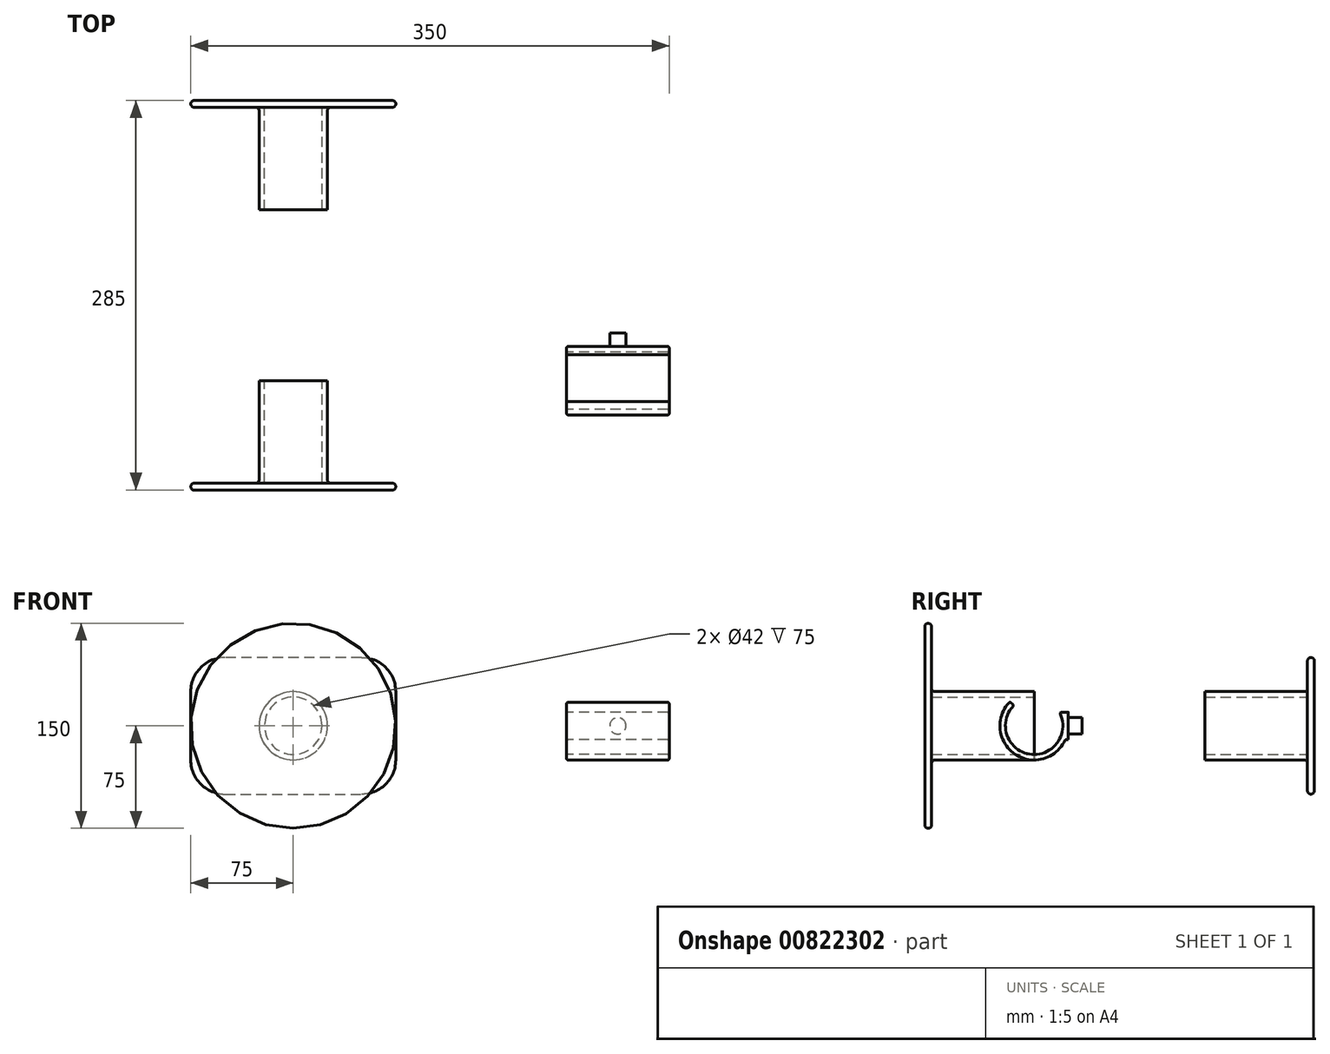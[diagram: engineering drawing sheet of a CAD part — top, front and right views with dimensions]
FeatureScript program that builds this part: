
annotation { "Feature Type Name" : "Feature", "Feature Type Description" : "" }
export const myFeature = defineFeature(function(context is Context, id is Id, definition is map)
    precondition{}
    {
        {
            var Q0;
            Q0=qCreatedBy(makeId("Front.planeOp"),FACE);
            var sketch = newSketch(context, id + "F0", { "sketchPlane" : qUnion([Q0])});
            skCircle(sketch, "E0", {"center": v(0, 0) * mm, "radius": 21 * mm});
            skCircle(sketch, "E1", {"center": v(0, 0) * mm, "radius": 25 * mm});
            skSolve(sketch);
        }
        {
            var Q0;
            Q0 = qSketchRegion(id + "F0", true);
            extrude(context, id + "F1", {"entities" : qUnion([Q0]), "depth" : 75 * mm, "offsetDistance" : 25 * mm});
        }
        {
            var Q0;
            Q0=makeQuery(id+"F1.opExtrude","CAP_FACE",FACE,{"disambiguationData":[OSD([sQuery(id+"F0.wireOp",EDGE,"E0"),sQuery(id+"F0.wireOp",EDGE,"E1")])],"isStart":false});
            var sketch = newSketch(context, id + "F2", { "sketchPlane" : qUnion([Q0])});
            skCircle(sketch, "E2", {"center": v(0, 0) * mm, "radius": 75 * mm});
            skSolve(sketch);
        }
        {
            var Q0;
            Q0 = qSketchRegion(id + "F2", true);
            extrude(context, id + "F3", {"entities" : qUnion([Q0]), "operationType" : NewBodyOperationType.ADD, "depth" : 5 * mm, "offsetDistance" : 25 * mm});
        }
        {
            var Q0;
            Q0=makeQuery(id+"F3.opExtrude","CAP_FACE",FACE,{"disambiguationData":[OSD([sQuery(id+"F2.wireOp",EDGE,"E2")])],"isStart":false});
            var Q1;
            {var subQ0=sQuery(id+"F2.wireOp",EDGE,"E2");Q1=makeQuery(id+"F3.boolean.opBoolean","SPLIT",FACE,{"disambiguationData":[TD([makeQuery(id+"F1.opExtrude","SWEPT_FACE",FACE,{"disambiguationData":[OSD([sQuery(id+"F0.wireOp",EDGE,"E1")])]})])],"derivedFrom":makeQuery(id+"F3.opExtrude","CAP_FACE",FACE,{"disambiguationData":[OSD([subQ0])],"isStart":true})});}
            fillet(context, id + "F4", {"entities" : qUnion([Q0, Q1]), "radius" : 2.5 * mm, "tangentPropagation" : true, "allowEdgeOverflow" : false});
        }
        {
            var Q0;
            Q0=qCreatedBy(makeId("Front.planeOp"),FACE);
            cPlane(context, id + "F5", {"entities" : qUnion([Q0]), "cplaneType" : CPlaneType.OFFSET, "offset" : 200 * mm, "oppositeDirection" : true, "width" : 150 * mm, "height" : 150 * mm});
        }
        {
            var Q0;
            Q0=qCreatedBy(id+"F5.planeOp",FACE);
            var sketch = newSketch(context, id + "F6", { "sketchPlane" : qUnion([Q0])});
            skCircle(sketch, "E3", {"center": v(0, 0) * mm, "radius": 21 * mm});
            skCircle(sketch, "E4", {"center": v(0, 0) * mm, "radius": 25 * mm});
            skSolve(sketch);
        }
        {
            var Q0;
            Q0 = qSketchRegion(id + "F6", true);
            extrude(context, id + "F7", {"entities" : qUnion([Q0]), "depth" : 75 * mm, "offsetDistance" : 25 * mm});
        }
        {
            var Q0;
            Q0=makeQuery(id+"F7.opExtrude","CAP_FACE",FACE,{"disambiguationData":[OSD([sQuery(id+"F6.wireOp",EDGE,"E3"),sQuery(id+"F6.wireOp",EDGE,"E4")])],"isStart":true});
            var sketch = newSketch(context, id + "F8", { "sketchPlane" : qUnion([Q0])});
            skLineSegment(sketch, "E5.bottom", {"start": v(-50, -50) * mm, "end": v(50, -50) * mm});
            skLineSegment(sketch, "E5.top", {"start": v(-50, 50) * mm, "end": v(50, 50) * mm});
            skLineSegment(sketch, "E5.left", {"start": v(-75, -25) * mm, "end": v(-75, 25) * mm});
            skLineSegment(sketch, "E5.right", {"start": v(75, -25) * mm, "end": v(75, 25) * mm});
            skPoint(sketch, "E5.middle", {"position": v(0, 0) * mm});
            skPoint(sketch, "E6.visualSharp", {"position": v(-75, 50) * mm});
            skArc(sketch, "E6.filletArc", {"start": v(-50, 50) * mm, "mid": v(-67.68, 42.68) * mm, "end": v(-75, 25) * mm});
            skPoint(sketch, "E7.visualSharp", {"position": v(-75, -50) * mm});
            skArc(sketch, "E7.filletArc", {"start": v(-75, -25) * mm, "mid": v(-67.68, -42.68) * mm, "end": v(-50, -50) * mm});
            skPoint(sketch, "E8.visualSharp", {"position": v(75, -50) * mm});
            skArc(sketch, "E8.filletArc", {"start": v(50, -50) * mm, "mid": v(67.68, -42.68) * mm, "end": v(75, -25) * mm});
            skPoint(sketch, "E9.visualSharp", {"position": v(75, 50) * mm});
            skArc(sketch, "E9.filletArc", {"start": v(75, 25) * mm, "mid": v(67.68, 42.68) * mm, "end": v(50, 50) * mm});
            skSolve(sketch);
        }
        {
            var Q0;
            Q0 = qSketchRegion(id + "F8", true);
            extrude(context, id + "F9", {"entities" : qUnion([Q0]), "operationType" : NewBodyOperationType.ADD, "depth" : 5 * mm, "offsetDistance" : 25 * mm});
        }
        {
            var Q0;
            Q0=makeQuery(id+"F9.opExtrude","CAP_FACE",FACE,{"disambiguationData":[OSD([sQuery(id+"F8.wireOp",EDGE,"E5.bottom"),sQuery(id+"F8.wireOp",EDGE,"E5.top"),sQuery(id+"F8.wireOp",EDGE,"E5.left"),sQuery(id+"F8.wireOp",EDGE,"E5.right"),sQuery(id+"F8.wireOp",EDGE,"E6.filletArc"),sQuery(id+"F8.wireOp",EDGE,"E7.filletArc"),sQuery(id+"F8.wireOp",EDGE,"E8.filletArc"),sQuery(id+"F8.wireOp",EDGE,"E9.filletArc")])],"isStart":false});
            var Q1;
            {var subQ0=sQuery(id+"F8.wireOp",EDGE,"E5.left");var subQ1=sQuery(id+"F8.wireOp",EDGE,"E5.top");var subQ2=sQuery(id+"F8.wireOp",EDGE,"E5.bottom");var subQ3=sQuery(id+"F8.wireOp",EDGE,"E5.right");var subQ4=sQuery(id+"F8.wireOp",EDGE,"E6.filletArc");var subQ5=sQuery(id+"F8.wireOp",EDGE,"E7.filletArc");var subQ6=sQuery(id+"F8.wireOp",EDGE,"E8.filletArc");var subQ7=sQuery(id+"F8.wireOp",EDGE,"E9.filletArc");Q1=makeQuery(id+"F9.boolean.opBoolean","SPLIT",FACE,{"disambiguationData":[TD([makeQuery(id+"F7.opExtrude","SWEPT_FACE",FACE,{"disambiguationData":[OSD([sQuery(id+"F6.wireOp",EDGE,"E4")])]})])],"derivedFrom":makeQuery(id+"F9.opExtrude","CAP_FACE",FACE,{"disambiguationData":[OSD([subQ2,subQ1,subQ0,subQ3,subQ4,subQ5,subQ6,subQ7])],"isStart":true})});}
            fillet(context, id + "F10", {"entities" : qUnion([Q0, Q1]), "radius" : 2.5 * mm, "tangentPropagation" : true, "allowEdgeOverflow" : false});
        }
        {
            var Q0;
            Q0=qCreatedBy(makeId("Right.planeOp"),FACE);
            cPlane(context, id + "F11", {"entities" : qUnion([Q0]), "cplaneType" : CPlaneType.OFFSET, "offset" : 200 * mm, "width" : 150 * mm, "height" : 150 * mm});
        }
        {
            var Q0;
            Q0=qCreatedBy(id+"F11.planeOp",FACE);
            var sketch = newSketch(context, id + "F12", { "sketchPlane" : qUnion([Q0])});
            skCircle(sketch, "E10", {"center": v(0, 0) * mm, "radius": 21 * mm});
            skCircle(sketch, "E11", {"center": v(0, 0) * mm, "radius": 25 * mm});
            skLineSegment(sketch, "E12", {"start": v(0, 0) * mm, "end": v(-25, 0) * mm});
            skLineSegment(sketch, "E13", {"start": v(0, 0) * mm, "end": v(-17.68, 17.68) * mm});
            skLineSegment(sketch, "E14", {"start": v(25, 0) * mm, "end": v(25, -10) * mm});
            skLineSegment(sketch, "E15", {"start": v(25, 0) * mm, "end": v(25, 10) * mm});
            skLineSegment(sketch, "E16", {"start": v(25, -10) * mm, "end": v(22.91, -10) * mm});
            skLineSegment(sketch, "E17", {"start": v(25, 10) * mm, "end": v(22.91, 10) * mm});
            skLineSegment(sketch, "E18", {"start": v(22.91, 10) * mm, "end": v(18.47, 10) * mm});
            skSolve(sketch);
        }
        {
            var Q0;
            {var subQ0=sQuery(id+"F12.wireOp",EDGE,"E14");Q0=makeQuery(id+"F12.imprint","IMPRINT",FACE,{"disambiguationData":[TD([[makeQuery(id+"F12.imprint","IMPRINT",EDGE,{"derivedFrom":subQ0}),-1.0]])]});}
            var Q1;
            {var subQ0=sQuery(id+"F12.wireOp",EDGE,"E15");Q1=makeQuery(id+"F12.imprint","IMPRINT",FACE,{"disambiguationData":[TD([[makeQuery(id+"F12.imprint","IMPRINT",EDGE,{"derivedFrom":subQ0}),1.0]])]});}
            var Q2;
            {var subQ5=sQuery(id+"F12.wireOp",EDGE,"E18");Q2=makeQuery(id+"F12.imprint","IMPRINT",FACE,{"disambiguationData":[TD([[makeQuery(id+"F12.imprint","IMPRINT",EDGE,{"derivedFrom":subQ5}),1.0]])]});}
            var Q3;
            {var subQ0=sQuery(id+"F12.wireOp",EDGE,"E13");var subQ1=sQuery(id+"F12.wireOp",EDGE,"E10");var subQ2=makeQuery(id+"F12.imprint","INTERSECT",VERTEX,{"derivedFrom":[subQ1,subQ0]});Q3=makeQuery(id+"F12.imprint","IMPRINT",FACE,{"disambiguationData":[TD([[makeQuery(id+"F12.imprint","IMPRINT",EDGE,{"disambiguationData":[TD([[subQ2,-1.0]])],"derivedFrom":subQ1}),-1.0]])]});}
            extrude(context, id + "F13", {"entities" : qUnion([Q0, Q1, Q2, Q3]), "depth" : 75 * mm, "offsetDistance" : 25 * mm});
        }
        {
            var Q0;
            Q0=makeQuery(id+"F13.opExtrude","SWEPT_FACE",FACE,{"disambiguationData":[OSD([sQuery(id+"F12.wireOp",EDGE,"E10")])]});
            var Q1;
            Q1=makeQuery(id+"F13.opExtrude","SWEPT_FACE",FACE,{"disambiguationData":[OSD([sQuery(id+"F12.wireOp",EDGE,"E11")])]});
            var Q2;
            Q2=makeQuery(id+"F13.opExtrude","CAP_FACE",FACE,{"disambiguationData":[OSD([sQuery(id+"F12.wireOp",EDGE,"E10"),sQuery(id+"F12.wireOp",EDGE,"E11"),sQuery(id+"F12.wireOp",EDGE,"E13"),sQuery(id+"F12.wireOp",EDGE,"E14"),sQuery(id+"F12.wireOp",EDGE,"E15"),sQuery(id+"F12.wireOp",EDGE,"E16"),sQuery(id+"F12.wireOp",EDGE,"E17"),sQuery(id+"F12.wireOp",EDGE,"E18")])],"isStart":false});
            var Q3;
            Q3=makeQuery(id+"F13.opExtrude","CAP_FACE",FACE,{"disambiguationData":[OSD([sQuery(id+"F12.wireOp",EDGE,"E10"),sQuery(id+"F12.wireOp",EDGE,"E11"),sQuery(id+"F12.wireOp",EDGE,"E13"),sQuery(id+"F12.wireOp",EDGE,"E14"),sQuery(id+"F12.wireOp",EDGE,"E15"),sQuery(id+"F12.wireOp",EDGE,"E16"),sQuery(id+"F12.wireOp",EDGE,"E17"),sQuery(id+"F12.wireOp",EDGE,"E18")])],"isStart":true});
            fillet(context, id + "F14", {"entities" : qUnion([Q0, Q1, Q2, Q3]), "radius" : 1 * mm, "tangentPropagation" : true, "allowEdgeOverflow" : false});
        }
        {
            var Q0;
            Q0=makeQuery(id+"F13.opExtrude","SWEPT_FACE",FACE,{"disambiguationData":[OSD([sQuery(id+"F12.wireOp",EDGE,"E14"),sQuery(id+"F12.wireOp",EDGE,"E15")])]});
            var sketch = newSketch(context, id + "F15", { "sketchPlane" : qUnion([Q0])});
            skCircle(sketch, "E19", {"center": v(-237.5, 0) * mm, "radius": 6 * mm});
            skPoint(sketch, "E19.centerSnap0", {"position": v(-201, 0) * mm});
            skPoint(sketch, "E19.centerSnap1", {"position": v(-237.5, 10) * mm});
            skSolve(sketch);
        }
        {
            var Q0;
            Q0 = qSketchRegion(id + "F15", true);
            extrude(context, id + "F16", {"entities" : qUnion([Q0]), "operationType" : NewBodyOperationType.ADD, "depth" : 10 * mm, "offsetDistance" : 25 * mm});
        }
    });
